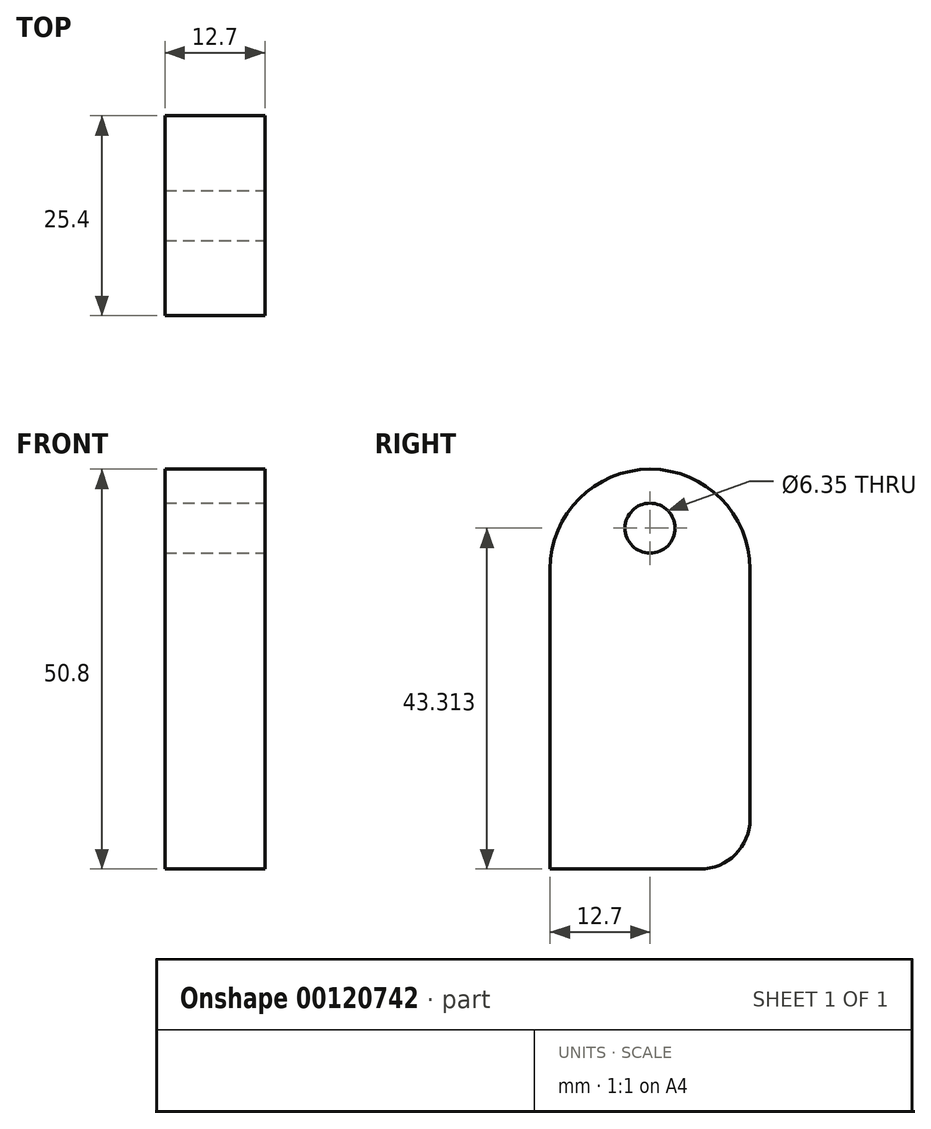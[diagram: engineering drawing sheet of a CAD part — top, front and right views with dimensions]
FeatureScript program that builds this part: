
annotation { "Feature Type Name" : "Feature", "Feature Type Description" : "" }
export const myFeature = defineFeature(function(context is Context, id is Id, definition is map)
    precondition{}
    {
        {
            var Q0;
            Q0=qCreatedBy(makeId("Front.planeOp"),FACE);
            var sketch = newSketch(context, id + "F0", { "sketchPlane" : qUnion([Q0])});
            skLineSegment(sketch, "E0.bottom", {"start": v(6.35, 25.4) * mm, "end": v(-6.35, 25.4) * mm});
            skLineSegment(sketch, "E0.top", {"start": v(6.35, -25.4) * mm, "end": v(-6.35, -25.4) * mm});
            skLineSegment(sketch, "E0.left", {"start": v(6.35, 25.4) * mm, "end": v(6.35, -25.4) * mm});
            skLineSegment(sketch, "E0.right", {"start": v(-6.35, 25.4) * mm, "end": v(-6.35, -25.4) * mm});
            skPoint(sketch, "E0.middle", {"position": v(0, 0) * mm});
            skSolve(sketch);
        }
        {
            var Q0;
            Q0 = qSketchRegion(id + "F0", true);
            extrude(context, id + "F1", {"entities" : qUnion([Q0]), "depth" : 25.4 * mm});
        }
        {
            var Q0;
            Q0=makeQuery(id+"F1.opExtrude","SWEPT_FACE",FACE,{"disambiguationData":[OSD([sQuery(id+"F0.wireOp",EDGE,"E0.left")])]});
            var sketch = newSketch(context, id + "F2", { "sketchPlane" : qUnion([Q0])});
            skCircle(sketch, "E1", {"center": v(-12.7, 17.91) * mm, "radius": 3.18 * mm});
            skSolve(sketch);
        }
        {
            var Q0;
            Q0 = qSketchRegion(id + "F2", true);
            extrude(context, id + "F3", {"entities" : qUnion([Q0]), "operationType" : NewBodyOperationType.REMOVE, "oppositeDirection" : true, "depth" : 25.4 * mm});
        }
        {
            var Q0;
            Q0=makeQuery(id+"F1.opExtrude","CAP_EDGE",EDGE,{"disambiguationData":[OSD([sQuery(id+"F0.wireOp",EDGE,"E0.bottom")])],"isStart":false});
            fillet(context, id + "F4", {"entities" : qUnion([Q0]), "radius" : 12.7 * mm, "tangentPropagation" : true, "allowEdgeOverflow" : false});
        }
        {
            var Q0;
            Q0=makeQuery(id+"F1.opExtrude","CAP_EDGE",EDGE,{"disambiguationData":[OSD([sQuery(id+"F0.wireOp",EDGE,"E0.bottom")])],"isStart":true});
            fillet(context, id + "F5", {"entities" : qUnion([Q0]), "radius" : 12.7 * mm, "tangentPropagation" : true, "allowEdgeOverflow" : false});
        }
        {
            var Q0;
            Q0=makeQuery(id+"F1.opExtrude","CAP_EDGE",EDGE,{"disambiguationData":[OSD([sQuery(id+"F0.wireOp",EDGE,"E0.top")])],"isStart":true});
            fillet(context, id + "F6", {"entities" : qUnion([Q0]), "radius" : 6.35 * mm, "tangentPropagation" : true, "allowEdgeOverflow" : false});
        }
    });
